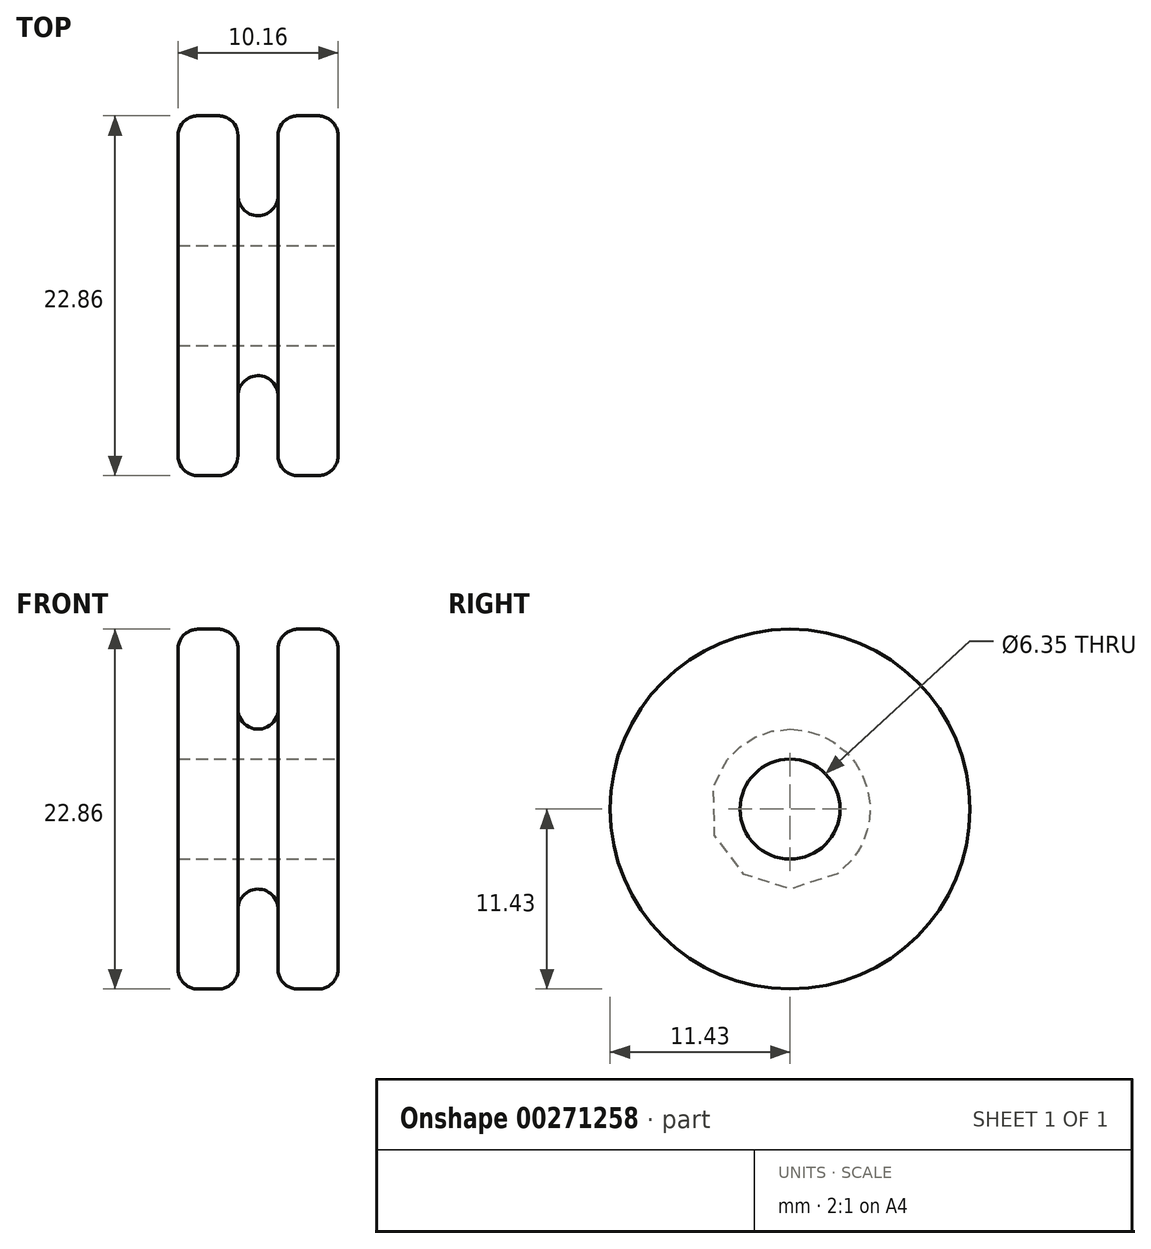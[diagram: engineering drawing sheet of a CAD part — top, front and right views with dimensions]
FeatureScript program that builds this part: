
annotation { "Feature Type Name" : "Feature", "Feature Type Description" : "" }
export const myFeature = defineFeature(function(context is Context, id is Id, definition is map)
    precondition{}
    {
        {
            var Q0;
            Q0=qCreatedBy(makeId("Front.planeOp"),FACE);
            var sketch = newSketch(context, id + "F0", { "sketchPlane" : qUnion([Q0])});
            skLineSegment(sketch, "E0", {"start": v(0, 0) * mm, "end": v(10.16, 0) * mm});
            skLineSegment(sketch, "E1", {"start": v(10.16, 0) * mm, "end": v(10.16, 11.43) * mm});
            skLineSegment(sketch, "E2", {"start": v(0, 11.43) * mm, "end": v(0, 0) * mm});
            skLineSegment(sketch, "E3", {"start": v(0, 11.43) * mm, "end": v(3.8, 11.43) * mm});
            skLineSegment(sketch, "E4", {"start": v(3.8, 11.43) * mm, "end": v(3.8, 5.08) * mm});
            skLineSegment(sketch, "E5", {"start": v(3.81, 5.08) * mm, "end": v(6.35, 5.08) * mm});
            skLineSegment(sketch, "E6", {"start": v(6.35, 5.08) * mm, "end": v(6.35, 11.43) * mm});
            skLineSegment(sketch, "E7", {"start": v(6.35, 11.43) * mm, "end": v(10.16, 11.43) * mm});
            skSolve(sketch);
        }
        {
            var Q0;
            Q0=makeQuery(id+"F0.imprint","IMPRINT",FACE,{"disambiguationData":[TD([[makeQuery(id+"F0.imprint","IMPRINT",EDGE,{"derivedFrom":sQuery(id+"F0.wireOp",EDGE,"E0")}),1.0]])]});
            var Q1;
            Q1=sQuery(id+"F0.wireOp",EDGE,"E0");
            revolve(context, id + "F1", {"entities" : qUnion([Q0]), "axis" : qUnion([Q1]), "revolveType" : RevolveType.FULL});
        }
        {
            var Q0;
            Q0=makeQuery(id+"F1.opRevolve","SWEPT_FACE",FACE,{"disambiguationData":[OSD([sQuery(id+"F0.wireOp",EDGE,"E1")])]});
            var sketch = newSketch(context, id + "F2", { "sketchPlane" : qUnion([Q0])});
            skCircle(sketch, "E8", {"center": v(0, 0) * mm, "radius": 3.18 * mm});
            skSolve(sketch);
        }
        {
            var Q0;
            Q0=makeQuery(id+"F2.imprint","IMPRINT",FACE,{"disambiguationData":[TD([[makeQuery(id+"F2.imprint","IMPRINT",EDGE,{"derivedFrom":sQuery(id+"F2.wireOp",EDGE,"E8")}),1.0]])]});
            extrude(context, id + "F3", {"entities" : qUnion([Q0]), "operationType" : NewBodyOperationType.REMOVE, "oppositeDirection" : true, "depth" : 25.4 * mm});
        }
        {
            var Q0;
            Q0=makeQuery(id+"F1.opRevolve","SWEPT_EDGE",EDGE,{"disambiguationData":[OSD([sQuery(id+"F0.wireOp",EDGE,"E5"),sQuery(id+"F0.wireOp",EDGE,"E6")])]});
            var Q1;
            Q1=makeQuery(id+"F1.opRevolve","SWEPT_EDGE",EDGE,{"disambiguationData":[OSD([sQuery(id+"F0.wireOp",EDGE,"E4"),sQuery(id+"F0.wireOp",EDGE,"E5")])]});
            var Q2;
            Q2=makeQuery(id+"F1.opRevolve","SWEPT_EDGE",EDGE,{"disambiguationData":[OSD([sQuery(id+"F0.wireOp",EDGE,"E3"),sQuery(id+"F0.wireOp",EDGE,"E4")])]});
            var Q3;
            Q3=makeQuery(id+"F1.opRevolve","SWEPT_EDGE",EDGE,{"disambiguationData":[OSD([sQuery(id+"F0.wireOp",EDGE,"E2"),sQuery(id+"F0.wireOp",EDGE,"E3")])]});
            var Q4;
            Q4=makeQuery(id+"F1.opRevolve","SWEPT_EDGE",EDGE,{"disambiguationData":[OSD([sQuery(id+"F0.wireOp",EDGE,"E1"),sQuery(id+"F0.wireOp",EDGE,"E7")])]});
            var Q5;
            Q5=makeQuery(id+"F1.opRevolve","SWEPT_EDGE",EDGE,{"disambiguationData":[OSD([sQuery(id+"F0.wireOp",EDGE,"E6"),sQuery(id+"F0.wireOp",EDGE,"E7")])]});
            fillet(context, id + "F4", {"entities" : qUnion([Q0, Q1, Q2, Q3, Q4, Q5]), "radius" : 1.27 * mm, "tangentPropagation" : true, "allowEdgeOverflow" : false});
        }
    });
